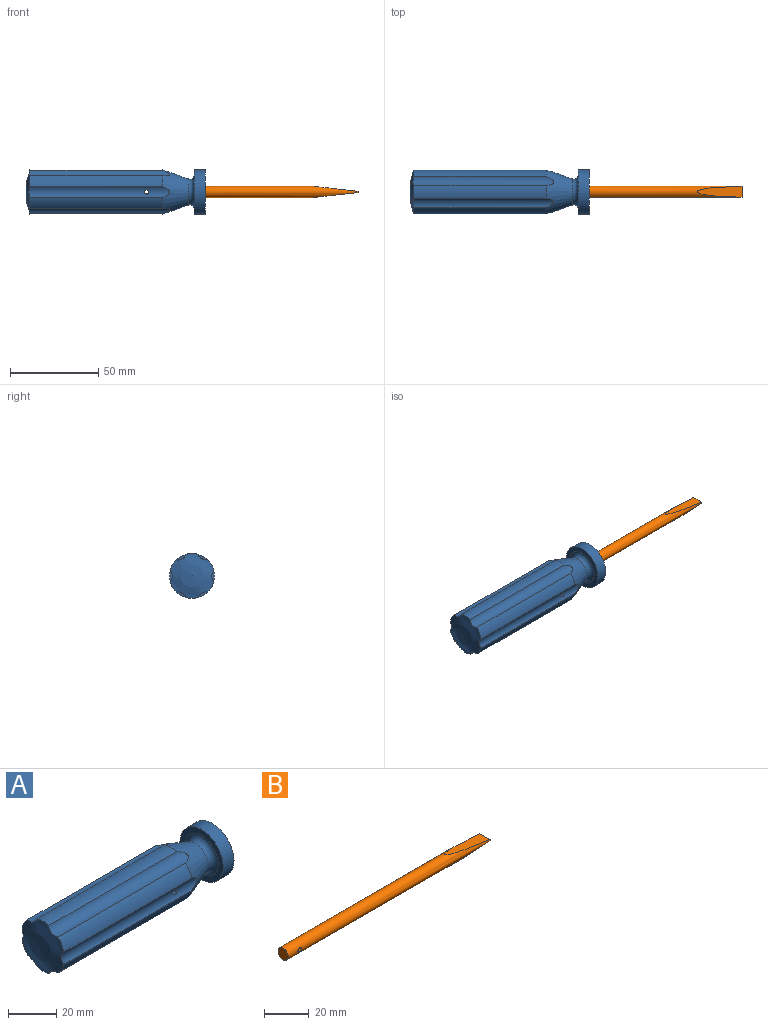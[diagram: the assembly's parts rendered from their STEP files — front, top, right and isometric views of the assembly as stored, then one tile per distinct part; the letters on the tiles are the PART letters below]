
ASSEMBLY  parts=2 mates=1
PART A: 22 faces, bbox 101.6x25.4x25.4 mm
  f0: cylinder r=12.7mm len=75.04mm, axis (1,0,0), area 526.2mm2, adj f7,f9,f14,f19
  f1: cylinder r=12.7mm len=75.04mm, axis (1,0,0), area 526.2mm2, adj f7,f9,f18,f19
  f2: cylinder r=12.7mm len=75.04mm, axis (1,0,0), area 526.2mm2, adj f7,f9,f17,f18
  f3: cylinder r=12.7mm len=75.04mm, axis (1,0,0), area 526.2mm2, adj f7,f9,f16,f17
  f4: cylinder r=12.7mm len=75.04mm, axis (1,0,0), area 526.2mm2, adj f7,f9,f15,f16
  f5: plane 25.4x25.4mm, normal (-1,0,0), area 207.2mm2, adj f6,f13
  f6: torus R=9.76mm, axis (1,0,0), area 244.8mm2, adj f5,f7
  f7: cone r=12.7mm half-angle=20deg, axis (-1,0,0), area 868.6mm2, adj f0,f1,f2,f3,f4,f6,f8,f14
  f8: cylinder r=12.7mm len=75.04mm, axis (1,0,0), area 526.2mm2, adj f7,f9,f14,f15
  f9: sphere r=38.1mm, area 480.8mm2, adj f0,f1,f2,f3,f4,f8,f14,f15
  f10: plane 6.35x6.35mm, normal (1,0,0), area 31.7mm2, adj f11
  f11: cylinder r=3.17mm len=40.64mm, axis (1,0,0), area 801.6mm2, adj f10,f12,f20,f21
  f12: plane 25.4x25.4mm, normal (1,0,0), area 475mm2, adj f11,f13
  f13: cylinder r=12.7mm len=25.4mm, axis (1,0,0), area 506.7mm2, adj f5,f12
  f14: cylinder r=4.83mm len=79.73mm, axis (1,0,0), area 528.2mm2, adj f0,f7,f8,f9
  f15: cylinder r=4.83mm len=79.73mm, axis (1,0,0), area 523.7mm2, adj f4,f7,f8,f9,f21
  f16: cylinder r=4.83mm len=79.73mm, axis (1,0,0), area 528.2mm2, adj f3,f4,f7,f9
  f17: cylinder r=4.83mm len=79.73mm, axis (1,0,0), area 528.2mm2, adj f2,f3,f7,f9
  f18: cylinder r=4.83mm len=79.73mm, axis (1,0,0), area 523.7mm2, adj f1,f2,f7,f9,f20
  f19: cylinder r=4.83mm len=79.73mm, axis (1,0,0), area 528.2mm2, adj f0,f1,f7,f9
  f20: cylinder r=1.19mm len=8.38mm, axis (0,-1,0), area 61.4mm2, adj f11,f18
  f21: cylinder r=1.19mm len=8.38mm, axis (0,-1,0), area 61.4mm2, adj f11,f15
PART B: 6 faces, bbox 127x6.4x6.4 mm
  f0: cylinder r=3.17mm len=127mm, axis (1,0,0), area 2224.3mm2, adj f1,f2,f3,f4,f5
  f1: plane 6.35x0.76mm, normal (1,0,0), area 4.8mm2, adj f0,f3,f4
  f2: plane 6.35x6.35mm, normal (-1,0,0), area 31.7mm2, adj f0
  f3: plane 25.4x6.3mm, normal (0.11,0,0.99), area 122.7mm2, adj f0,f1
  f4: plane 25.4x6.3mm, normal (0.11,0,-0.99), area 122.7mm2, adj f0,f1
  f5: cylinder r=1.19mm len=6.35mm, axis (0,-1,0), area 45.9mm2, adj f0
PLACE A t=(-37.41,-29.74,27.3)mm
PLACE B t=(48.95,-29.56,27.33)mm
MATE planar B.f0 <-> A.f0  axis (-1,0,0) through (-78.05,-29.56,27.33)mm
